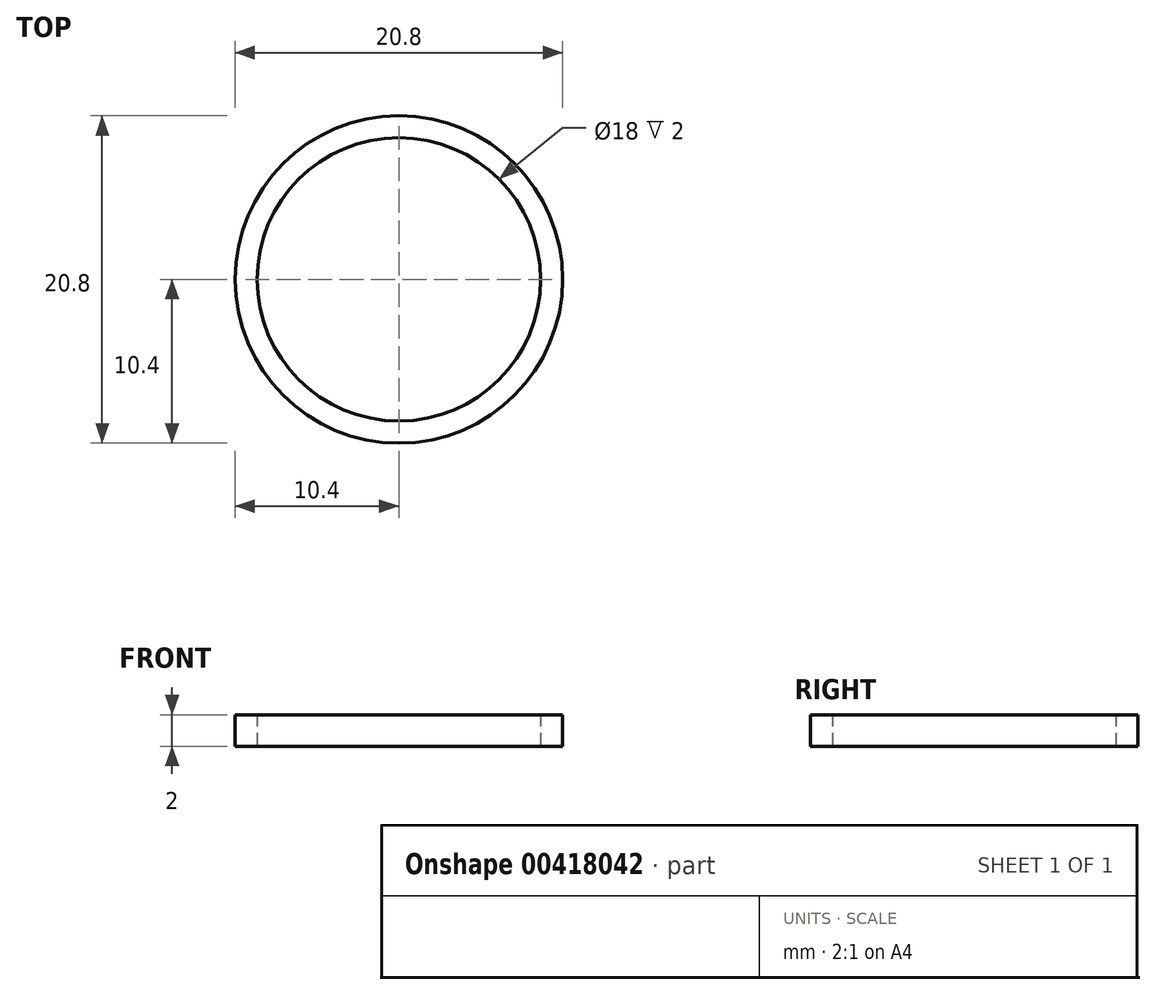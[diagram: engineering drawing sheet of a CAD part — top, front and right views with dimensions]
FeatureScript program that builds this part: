
annotation { "Feature Type Name" : "Feature", "Feature Type Description" : "" }
export const myFeature = defineFeature(function(context is Context, id is Id, definition is map)
    precondition{}
    {
        {
            var Q0;
            Q0=qCreatedBy(makeId("Top.planeOp"),FACE);
            var sketch = newSketch(context, id + "F0", { "sketchPlane" : qUnion([Q0])});
            skCircle(sketch, "E0", {"center": v(0, 0) * mm, "radius": 10.4 * mm});
            skCircle(sketch, "E1", {"center": v(0, 0) * mm, "radius": 9 * mm});
            skSolve(sketch);
        }
        {
            var Q0;
            Q0 = qSketchRegion(id + "F0", true);
            extrude(context, id + "F1", {"entities" : qUnion([Q0]), "endBound" : BoundingType.SYMMETRIC, "depth" : 2 * mm});
        }
    });
